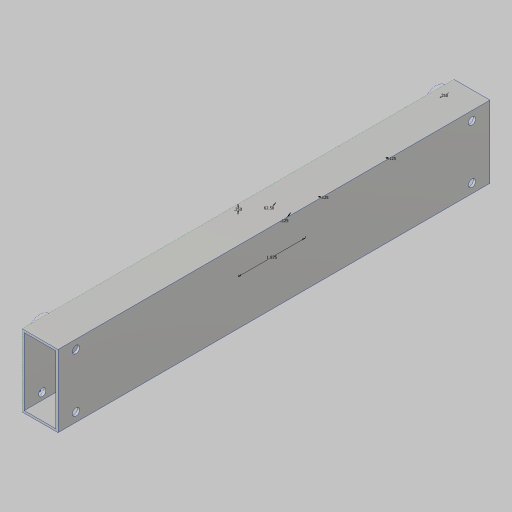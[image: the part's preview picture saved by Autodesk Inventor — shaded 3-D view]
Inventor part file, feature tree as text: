
AUTODESK INVENTOR PART (.ipt)
format: ipt  version: 2023.5 (Build 275446000, 446)  size: 140,288 bytes
history: native  units: in
note: dims shown in document units (in); Inventor stores cm internally (conversion verified against a paired STEP export)
features: sketch x2, extrude x1, hole x1, projected_geometry x1
ambient origin geometry x8: Origin, YZ Plane, XZ Plane, XY Plane, X Axis, Y Axis, Z Axis, Center Point
bodies: Solid1 (feature_tree)
feature tree (5):
  extrude  "Extrusion1"  Depth=0.5in
  hole  "Hole1"  [1 undecoded]
  sketch  "Sketch3"  dims[d6=0.5in d7=1.5in d8=0.201in d9=0.75in d10=0.385in d11=0.25in d12=0.5635in d13=1.0in d14=0.8108in d15=0.25in d16=0.25in d19=0.4295in d20=1.1811in d22=1.875in d23=0.3937in d25=1.0in d27=0.125in d28=0.125in d29=0.125in]
  sketch  "Sketch2"  dims[d4=0.0in d5=0.5in]
  projected_geometry  "Projected Loop1"
note: 1 required parameter value undecoded (feature->parameter linkage not recoverable at this tier; creation-order binding heuristic only, values carry confidence <= 0.55)
